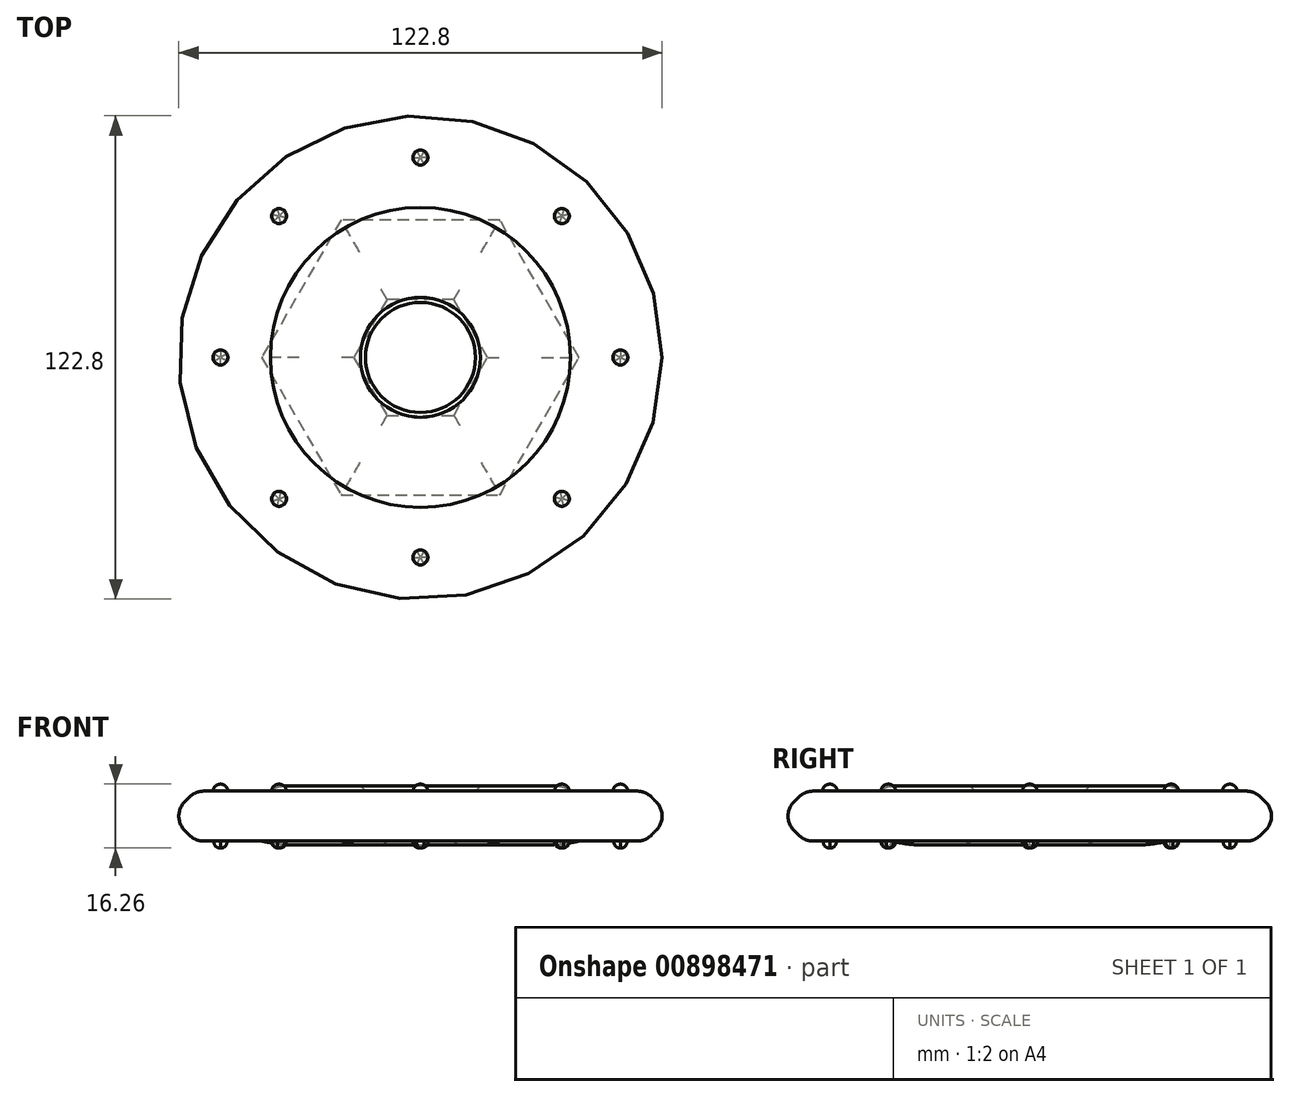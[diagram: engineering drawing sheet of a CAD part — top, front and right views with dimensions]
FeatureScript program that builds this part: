
annotation { "Feature Type Name" : "Feature", "Feature Type Description" : "" }
export const myFeature = defineFeature(function(context is Context, id is Id, definition is map)
    precondition{}
    {
        {
            var Q0;
            Q0=qCreatedBy(makeId("Top.planeOp"),FACE);
            var sketch = newSketch(context, id + "F0", { "sketchPlane" : qUnion([Q0])});
            skCircle(sketch, "E0", {"center": v(0, 0) * mm, "radius": 63.5 * mm});
            skSolve(sketch);
        }
        {
            var Q0;
            Q0=makeQuery(id+"F0.imprint","IMPRINT",FACE,{"disambiguationData":[TD([[makeQuery(id+"F0.imprint","IMPRINT",EDGE,{"derivedFrom":sQuery(id+"F0.wireOp",EDGE,"E0")}),1.0]])]});
            extrude(context, id + "F1", {"entities" : qUnion([Q0]), "depth" : 12.7 * mm, "offsetDistance" : 25.4 * mm});
        }
        {
            var Q0;
            Q0=makeQuery(id+"F1.opExtrude","CAP_FACE",FACE,{"disambiguationData":[OSD([sQuery(id+"F0.wireOp",EDGE,"E0")])],"isStart":false});
            var Q1;
            Q1=makeQuery(id+"F1.opExtrude","CAP_EDGE",EDGE,{"disambiguationData":[OSD([sQuery(id+"F0.wireOp",EDGE,"E0")])],"isStart":true});
            chamfer(context, id + "F2", {"entities" : qUnion([Q0, Q1]), "width" : 6.35 * mm, "tangentPropagation" : true});
        }
        {
            var Q0;
            Q0=makeQuery(id+"F1.opExtrude","CAP_FACE",FACE,{"disambiguationData":[OSD([sQuery(id+"F0.wireOp",EDGE,"E0")])],"isStart":false});
            fillet(context, id + "F3", {"entities" : qUnion([Q0]), "radius" : 5.08 * mm, "tangentPropagation" : true, "allowEdgeOverflow" : false});
        }
        {
            var Q0;
            {var subQ0=sQuery(id+"F0.wireOp",EDGE,"E0");Q0=makeQuery(id+"F2.opChamfer","BLEND_EDGE",EDGE,{"blendedFrom":[makeQuery(id+"F1.opExtrude","CAP_EDGE",EDGE,{"disambiguationData":[OSD([subQ0])],"isStart":true}),makeQuery(id+"F1.opExtrude","CAP_FACE",FACE,{"disambiguationData":[OSD([subQ0])],"isStart":true})],"blendedInto":[makeQuery(id+"F1.opExtrude","CAP_FACE",FACE,{"disambiguationData":[OSD([subQ0])],"isStart":true})]});}
            fillet(context, id + "F4", {"entities" : qUnion([Q0]), "radius" : 5.08 * mm, "tangentPropagation" : true, "allowEdgeOverflow" : false});
        }
        {
            var Q0;
            Q0=makeQuery(id+"F1.opExtrude","CAP_FACE",FACE,{"disambiguationData":[OSD([sQuery(id+"F0.wireOp",EDGE,"E0")])],"isStart":false});
            var sketch = newSketch(context, id + "F5", { "sketchPlane" : qUnion([Q0])});
            skLineSegment(sketch, "E1", {"start": v(0, 0) * mm, "end": v(0, 50.8) * mm, "construction": true});
            skCircle(sketch, "E2", {"center": v(0, 0) * mm, "radius": 50.8 * mm, "construction": true});
            skCircle(sketch, "E3", {"center": v(0, 50.8) * mm, "radius": 1.9 * mm});
            skLineSegment(sketch, "E4", {"start": v(-50.8, 0) * mm, "end": v(50.8, 0) * mm, "construction": true});
            skLineSegment(sketch, "E5", {"start": v(0, 0) * mm, "end": v(0, -50.8) * mm, "construction": true});
            skCircle(sketch, "E6", {"center": v(-50.8, 0) * mm, "radius": 1.9 * mm});
            skCircle(sketch, "E7", {"center": v(50.8, 0) * mm, "radius": 1.9 * mm});
            skCircle(sketch, "E8", {"center": v(0, -50.8) * mm, "radius": 1.9 * mm});
            skLineSegment(sketch, "E9", {"start": v(0, 0) * mm, "end": v(35.92, 35.92) * mm, "construction": true});
            skLineSegment(sketch, "E10", {"start": v(0, 0) * mm, "end": v(-35.92, 35.92) * mm, "construction": true});
            skLineSegment(sketch, "E11", {"start": v(-35.92, -35.92) * mm, "end": v(0, 0) * mm, "construction": true});
            skLineSegment(sketch, "E12", {"start": v(35.92, -35.92) * mm, "end": v(0, 0) * mm, "construction": true});
            skCircle(sketch, "E13", {"center": v(-35.92, 35.92) * mm, "radius": 1.9 * mm});
            skCircle(sketch, "E14", {"center": v(35.92, 35.92) * mm, "radius": 1.9 * mm});
            skCircle(sketch, "E15", {"center": v(35.92, -35.92) * mm, "radius": 1.9 * mm});
            skCircle(sketch, "E16", {"center": v(-35.92, -35.92) * mm, "radius": 1.9 * mm});
            skSolve(sketch);
        }
        {
            var Q0;
            Q0 = qSketchRegion(id + "F5", true);
            extrude(context, id + "F6", {"entities" : qUnion([Q0]), "operationType" : NewBodyOperationType.ADD, "depth" : 1.78 * mm, "offsetDistance" : 25.4 * mm});
        }
        {
            var Q0;
            Q0=makeQuery(id+"F6.opExtrude","CAP_EDGE",EDGE,{"disambiguationData":[OSD([sQuery(id+"F5.wireOp",EDGE,"E16")])],"isStart":false});
            var Q1;
            Q1=makeQuery(id+"F6.opExtrude","CAP_EDGE",EDGE,{"disambiguationData":[OSD([sQuery(id+"F5.wireOp",EDGE,"E6")])],"isStart":false});
            var Q2;
            Q2=makeQuery(id+"F6.opExtrude","CAP_EDGE",EDGE,{"disambiguationData":[OSD([sQuery(id+"F5.wireOp",EDGE,"E13")])],"isStart":false});
            var Q3;
            Q3=makeQuery(id+"F6.opExtrude","CAP_EDGE",EDGE,{"disambiguationData":[OSD([sQuery(id+"F5.wireOp",EDGE,"E3")])],"isStart":false});
            var Q4;
            Q4=makeQuery(id+"F6.opExtrude","CAP_EDGE",EDGE,{"disambiguationData":[OSD([sQuery(id+"F5.wireOp",EDGE,"E14")])],"isStart":false});
            var Q5;
            Q5=makeQuery(id+"F6.opExtrude","CAP_EDGE",EDGE,{"disambiguationData":[OSD([sQuery(id+"F5.wireOp",EDGE,"E7")])],"isStart":false});
            var Q6;
            Q6=makeQuery(id+"F6.opExtrude","CAP_EDGE",EDGE,{"disambiguationData":[OSD([sQuery(id+"F5.wireOp",EDGE,"E15")])],"isStart":false});
            var Q7;
            Q7=makeQuery(id+"F6.opExtrude","CAP_EDGE",EDGE,{"disambiguationData":[OSD([sQuery(id+"F5.wireOp",EDGE,"E8")])],"isStart":false});
            fillet(context, id + "F7", {"entities" : qUnion([Q0, Q1, Q2, Q3, Q4, Q5, Q6, Q7]), "radius" : 1.9 * mm, "tangentPropagation" : true, "allowEdgeOverflow" : false});
        }
        {
            var Q0;
            Q0=makeQuery(id+"F1.opExtrude","CAP_FACE",FACE,{"disambiguationData":[OSD([sQuery(id+"F0.wireOp",EDGE,"E0")])],"isStart":false});
            var sketch = newSketch(context, id + "F8", { "sketchPlane" : qUnion([Q0])});
            skCircle(sketch, "E17", {"center": v(0, 0) * mm, "radius": 38.1 * mm});
            skCircle(sketch, "E18", {"center": v(0, 0) * mm, "radius": 19.05 * mm});
            skSolve(sketch);
        }
        {
            var Q0;
            Q0 = qSketchRegion(id + "F8", true);
            extrude(context, id + "F9", {"entities" : qUnion([Q0]), "operationType" : NewBodyOperationType.ADD, "depth" : 1.27 * mm, "offsetDistance" : 25.4 * mm});
        }
        {
            var Q0;
            Q0=makeQuery(id+"F1.opExtrude","CAP_FACE",FACE,{"disambiguationData":[OSD([sQuery(id+"F0.wireOp",EDGE,"E0")])],"isStart":true});
            var sketch = newSketch(context, id + "F10", { "sketchPlane" : qUnion([Q0])});
            skCircle(sketch, "E19.cCircle", {"center": v(0, 0) * mm, "radius": 34.91 * mm, "construction": true});
            skLineSegment(sketch, "E19.0", {"start": v(20.16, -34.91) * mm, "end": v(-20.16, -34.91) * mm});
            skLineSegment(sketch, "E19.1", {"start": v(-20.16, -34.91) * mm, "end": v(-40.31, 0) * mm});
            skLineSegment(sketch, "E19.2", {"start": v(-40.31, 0) * mm, "end": v(-20.16, 34.91) * mm});
            skLineSegment(sketch, "E19.3", {"start": v(-20.16, 34.91) * mm, "end": v(20.16, 34.91) * mm});
            skLineSegment(sketch, "E19.4", {"start": v(20.16, 34.91) * mm, "end": v(40.31, 0) * mm});
            skLineSegment(sketch, "E19.5", {"start": v(40.31, 0) * mm, "end": v(20.16, -34.91) * mm});
            skPoint(sketch, "E19.0.midPoint", {"position": v(0, -34.91) * mm});
            skCircle(sketch, "E20.cCircle", {"center": v(0, 0) * mm, "radius": 14.71 * mm, "construction": true});
            skLineSegment(sketch, "E20.0", {"start": v(8.5, -14.71) * mm, "end": v(-8.5, -14.71) * mm});
            skLineSegment(sketch, "E20.1", {"start": v(-8.5, -14.71) * mm, "end": v(-17, 0) * mm});
            skLineSegment(sketch, "E20.2", {"start": v(-17, 0) * mm, "end": v(-8.5, 14.71) * mm});
            skLineSegment(sketch, "E20.3", {"start": v(-8.5, 14.71) * mm, "end": v(8.5, 14.71) * mm});
            skLineSegment(sketch, "E20.4", {"start": v(8.5, 14.71) * mm, "end": v(17, 0) * mm});
            skLineSegment(sketch, "E20.5", {"start": v(17, 0) * mm, "end": v(8.5, -14.71) * mm});
            skPoint(sketch, "E20.0.midPoint", {"position": v(0, -14.71) * mm});
            skSolve(sketch);
        }
        {
            var Q0;
            Q0 = qSketchRegion(id + "F10", true);
            extrude(context, id + "F11", {"entities" : qUnion([Q0]), "operationType" : NewBodyOperationType.ADD, "depth" : 1.02 * mm, "offsetDistance" : 25.4 * mm});
        }
        {
            var Q0;
            Q0=makeQuery(id+"F11.opExtrude","CAP_EDGE",EDGE,{"disambiguationData":[OSD([sQuery(id+"F10.wireOp",EDGE,"E19.1")])],"isStart":false});
            var Q1;
            Q1=makeQuery(id+"F11.opExtrude","CAP_EDGE",EDGE,{"disambiguationData":[OSD([sQuery(id+"F10.wireOp",EDGE,"E19.0")])],"isStart":false});
            var Q2;
            Q2=makeQuery(id+"F11.opExtrude","CAP_EDGE",EDGE,{"disambiguationData":[OSD([sQuery(id+"F10.wireOp",EDGE,"E19.5")])],"isStart":false});
            var Q3;
            Q3=makeQuery(id+"F11.opExtrude","CAP_EDGE",EDGE,{"disambiguationData":[OSD([sQuery(id+"F10.wireOp",EDGE,"E19.4")])],"isStart":false});
            var Q4;
            Q4=makeQuery(id+"F11.opExtrude","CAP_EDGE",EDGE,{"disambiguationData":[OSD([sQuery(id+"F10.wireOp",EDGE,"E19.3")])],"isStart":false});
            var Q5;
            Q5=makeQuery(id+"F11.opExtrude","CAP_EDGE",EDGE,{"disambiguationData":[OSD([sQuery(id+"F10.wireOp",EDGE,"E19.2")])],"isStart":false});
            fillet(context, id + "F12", {"entities" : qUnion([Q0, Q1, Q2, Q3, Q4, Q5]), "radius" : 33.78 * mm, "tangentPropagation" : true, "allowEdgeOverflow" : false});
        }
        {
            var Q0;
            Q0=makeQuery(id+"F9.opExtrude","CAP_EDGE",EDGE,{"disambiguationData":[OSD([sQuery(id+"F8.wireOp",EDGE,"E17")])],"isStart":false});
            fillet(context, id + "F13", {"entities" : qUnion([Q0]), "radius" : 5.08 * mm, "tangentPropagation" : true, "allowEdgeOverflow" : false});
        }
        {
            var Q0;
            Q0=makeQuery(id+"F9.boolean.opBoolean","SPLIT",FACE,{"disambiguationData":[TD([makeQuery(id+"F9.opExtrude","SWEPT_FACE",FACE,{"disambiguationData":[OSD([sQuery(id+"F8.wireOp",EDGE,"E18")])]})])],"derivedFrom":makeQuery(id+"F1.opExtrude","CAP_FACE",FACE,{"disambiguationData":[OSD([sQuery(id+"F0.wireOp",EDGE,"E0")])],"isStart":false})});
            chamfer(context, id + "F14", {"entities" : qUnion([Q0]), "width" : 5.08 * mm, "tangentPropagation" : true});
        }
        {
            var Q0;
            {var subQ0=sQuery(id+"F0.wireOp",EDGE,"E0");Q0=makeQuery(id+"F11.boolean.opBoolean","SPLIT",FACE,{"disambiguationData":[TD([makeQuery(id+"F4.opFillet","BLEND_FACE",FACE,{"disambiguationData":[OSD([subQ0])]})])],"derivedFrom":makeQuery(id+"F1.opExtrude","CAP_FACE",FACE,{"disambiguationData":[OSD([subQ0])],"isStart":true})});}
            var sketch = newSketch(context, id + "F15", { "sketchPlane" : qUnion([Q0])});
            skCircle(sketch, "E21", {"center": v(0, 0) * mm, "radius": 50.8 * mm, "construction": true});
            skCircle(sketch, "E22.cCircle", {"center": v(0, 50.8) * mm, "radius": 1.65 * mm, "construction": true});
            skLineSegment(sketch, "E22.0", {"start": v(0.95, 49.15) * mm, "end": v(-0.95, 49.15) * mm});
            skLineSegment(sketch, "E22.1", {"start": v(-0.95, 49.15) * mm, "end": v(-1.9, 50.8) * mm});
            skLineSegment(sketch, "E22.2", {"start": v(-1.9, 50.8) * mm, "end": v(-0.95, 52.45) * mm});
            skLineSegment(sketch, "E22.3", {"start": v(-0.95, 52.45) * mm, "end": v(0.95, 52.45) * mm});
            skLineSegment(sketch, "E22.4", {"start": v(0.95, 52.45) * mm, "end": v(1.9, 50.8) * mm});
            skLineSegment(sketch, "E22.5", {"start": v(1.9, 50.8) * mm, "end": v(0.95, 49.15) * mm});
            skPoint(sketch, "E22.0.midPoint", {"position": v(0, 49.15) * mm});
            skCircle(sketch, "E23.cCircle", {"center": v(35.92, 35.92) * mm, "radius": 1.65 * mm, "construction": true});
            skLineSegment(sketch, "E23.0", {"start": v(35.43, 34.08) * mm, "end": v(34.08, 35.43) * mm});
            skLineSegment(sketch, "E23.1", {"start": v(34.08, 35.43) * mm, "end": v(34.57, 37.27) * mm});
            skLineSegment(sketch, "E23.2", {"start": v(34.57, 37.27) * mm, "end": v(36.41, 37.76) * mm});
            skLineSegment(sketch, "E23.3", {"start": v(36.41, 37.76) * mm, "end": v(37.76, 36.41) * mm});
            skLineSegment(sketch, "E23.4", {"start": v(37.76, 36.41) * mm, "end": v(37.27, 34.57) * mm});
            skLineSegment(sketch, "E23.5", {"start": v(37.27, 34.57) * mm, "end": v(35.43, 34.08) * mm});
            skPoint(sketch, "E23.0.midPoint", {"position": v(34.75, 34.75) * mm});
            skCircle(sketch, "E24.cCircle", {"center": v(50.8, 0) * mm, "radius": 1.65 * mm, "construction": true});
            skLineSegment(sketch, "E24.0", {"start": v(49.15, -0.95) * mm, "end": v(49.15, 0.95) * mm});
            skLineSegment(sketch, "E24.1", {"start": v(49.15, 0.95) * mm, "end": v(50.8, 1.9) * mm});
            skLineSegment(sketch, "E24.2", {"start": v(50.8, 1.9) * mm, "end": v(52.45, 0.95) * mm});
            skLineSegment(sketch, "E24.3", {"start": v(52.45, 0.95) * mm, "end": v(52.45, -0.95) * mm});
            skLineSegment(sketch, "E24.4", {"start": v(52.45, -0.95) * mm, "end": v(50.8, -1.9) * mm});
            skLineSegment(sketch, "E24.5", {"start": v(50.8, -1.9) * mm, "end": v(49.15, -0.95) * mm});
            skPoint(sketch, "E24.0.midPoint", {"position": v(49.15, 0) * mm});
            skPoint(sketch, "E25.0.midPoint", {"position": v(34.75, -32.79) * mm});
            skCircle(sketch, "E26.cCircle", {"center": v(-50.8, 0) * mm, "radius": 1.65 * mm, "construction": true});
            skLineSegment(sketch, "E26.0", {"start": v(-49.15, 0.95) * mm, "end": v(-49.15, -0.95) * mm});
            skLineSegment(sketch, "E26.1", {"start": v(-49.15, -0.95) * mm, "end": v(-50.8, -1.9) * mm});
            skLineSegment(sketch, "E26.2", {"start": v(-50.8, -1.9) * mm, "end": v(-52.45, -0.95) * mm});
            skLineSegment(sketch, "E26.3", {"start": v(-52.45, -0.95) * mm, "end": v(-52.45, 0.95) * mm});
            skLineSegment(sketch, "E26.4", {"start": v(-52.45, 0.95) * mm, "end": v(-50.8, 1.9) * mm});
            skLineSegment(sketch, "E26.5", {"start": v(-50.8, 1.9) * mm, "end": v(-49.15, 0.95) * mm});
            skPoint(sketch, "E26.0.midPoint", {"position": v(-49.15, 0) * mm});
            skCircle(sketch, "E27.cCircle", {"center": v(0, -50.8) * mm, "radius": 1.65 * mm, "construction": true});
            skLineSegment(sketch, "E27.0", {"start": v(-0.95, -49.15) * mm, "end": v(0.95, -49.15) * mm});
            skLineSegment(sketch, "E27.1", {"start": v(0.95, -49.15) * mm, "end": v(1.9, -50.8) * mm});
            skLineSegment(sketch, "E27.2", {"start": v(1.9, -50.8) * mm, "end": v(0.95, -52.45) * mm});
            skLineSegment(sketch, "E27.3", {"start": v(0.95, -52.45) * mm, "end": v(-0.95, -52.45) * mm});
            skLineSegment(sketch, "E27.4", {"start": v(-0.95, -52.45) * mm, "end": v(-1.9, -50.8) * mm});
            skLineSegment(sketch, "E27.5", {"start": v(-1.9, -50.8) * mm, "end": v(-0.95, -49.15) * mm});
            skPoint(sketch, "E27.0.midPoint", {"position": v(0, -49.15) * mm});
            skLineSegment(sketch, "E28", {"start": v(-1.9, -50.8) * mm, "end": v(1.9, -50.8) * mm, "construction": true});
            skCircle(sketch, "E29.cCircle", {"center": v(35.92, -35.92) * mm, "radius": 1.65 * mm, "construction": true});
            skLineSegment(sketch, "E29.0", {"start": v(37.76, -36.41) * mm, "end": v(36.41, -37.76) * mm});
            skLineSegment(sketch, "E29.1", {"start": v(36.41, -37.76) * mm, "end": v(34.57, -37.27) * mm});
            skLineSegment(sketch, "E29.2", {"start": v(34.57, -37.27) * mm, "end": v(34.08, -35.43) * mm});
            skLineSegment(sketch, "E29.3", {"start": v(34.08, -35.43) * mm, "end": v(35.43, -34.08) * mm});
            skLineSegment(sketch, "E29.4", {"start": v(35.43, -34.08) * mm, "end": v(37.27, -34.57) * mm});
            skLineSegment(sketch, "E29.5", {"start": v(37.27, -34.57) * mm, "end": v(37.76, -36.41) * mm});
            skPoint(sketch, "E29.0.midPoint", {"position": v(37.09, -37.09) * mm});
            skPoint(sketch, "E30.0.midPoint", {"position": v(-34.7, -37.03) * mm});
            skPoint(sketch, "E30.0.midPoint.positionSnap0", {"position": v(-34.7, -40.48) * mm});
            skCircle(sketch, "E31.cCircle", {"center": v(-35.92, 35.92) * mm, "radius": 1.65 * mm, "construction": true});
            skLineSegment(sketch, "E31.0", {"start": v(-34.1, 35.37) * mm, "end": v(-35.49, 34.07) * mm});
            skLineSegment(sketch, "E31.1", {"start": v(-35.49, 34.07) * mm, "end": v(-37.3, 34.62) * mm});
            skLineSegment(sketch, "E31.2", {"start": v(-37.3, 34.62) * mm, "end": v(-37.74, 36.47) * mm});
            skLineSegment(sketch, "E31.3", {"start": v(-37.74, 36.47) * mm, "end": v(-36.36, 37.78) * mm});
            skLineSegment(sketch, "E31.4", {"start": v(-36.36, 37.78) * mm, "end": v(-34.53, 37.23) * mm});
            skLineSegment(sketch, "E31.5", {"start": v(-34.53, 37.23) * mm, "end": v(-34.1, 35.37) * mm});
            skPoint(sketch, "E31.0.midPoint", {"position": v(-34.8, 34.72) * mm});
            skCircle(sketch, "E32.cCircle", {"center": v(-35.92, -35.92) * mm, "radius": 1.65 * mm, "construction": true});
            skLineSegment(sketch, "E32.0", {"start": v(-35.44, -34.08) * mm, "end": v(-34.09, -35.41) * mm});
            skLineSegment(sketch, "E32.1", {"start": v(-34.09, -35.41) * mm, "end": v(-34.56, -37.26) * mm});
            skLineSegment(sketch, "E32.2", {"start": v(-34.56, -37.26) * mm, "end": v(-36.4, -37.77) * mm});
            skLineSegment(sketch, "E32.3", {"start": v(-36.4, -37.77) * mm, "end": v(-37.76, -36.43) * mm});
            skLineSegment(sketch, "E32.4", {"start": v(-37.76, -36.43) * mm, "end": v(-37.28, -34.59) * mm});
            skLineSegment(sketch, "E32.5", {"start": v(-37.28, -34.59) * mm, "end": v(-35.44, -34.08) * mm});
            skPoint(sketch, "E32.0.midPoint", {"position": v(-34.76, -34.74) * mm});
            skSolve(sketch);
        }
        {
            var Q0;
            Q0 = qSketchRegion(id + "F15", true);
            extrude(context, id + "F16", {"entities" : qUnion([Q0]), "operationType" : NewBodyOperationType.ADD, "depth" : 1.78 * mm, "offsetDistance" : 25.4 * mm});
        }
        {
            var Q0;
            Q0=makeQuery(id+"F16.opExtrude","CAP_FACE",FACE,{"disambiguationData":[OSD([sQuery(id+"F15.wireOp",EDGE,"E27.0"),sQuery(id+"F15.wireOp",EDGE,"E27.1"),sQuery(id+"F15.wireOp",EDGE,"E27.2"),sQuery(id+"F15.wireOp",EDGE,"E27.3"),sQuery(id+"F15.wireOp",EDGE,"E27.4"),sQuery(id+"F15.wireOp",EDGE,"E27.5")])],"isStart":false});
            var Q1;
            Q1=makeQuery(id+"F16.opExtrude","CAP_FACE",FACE,{"disambiguationData":[OSD([sQuery(id+"F15.wireOp",EDGE,"E29.0"),sQuery(id+"F15.wireOp",EDGE,"E29.1"),sQuery(id+"F15.wireOp",EDGE,"E29.2"),sQuery(id+"F15.wireOp",EDGE,"E29.3"),sQuery(id+"F15.wireOp",EDGE,"E29.4"),sQuery(id+"F15.wireOp",EDGE,"E29.5")])],"isStart":false});
            var Q2;
            Q2=makeQuery(id+"F16.opExtrude","CAP_FACE",FACE,{"disambiguationData":[OSD([sQuery(id+"F15.wireOp",EDGE,"E24.0"),sQuery(id+"F15.wireOp",EDGE,"E24.1"),sQuery(id+"F15.wireOp",EDGE,"E24.2"),sQuery(id+"F15.wireOp",EDGE,"E24.3"),sQuery(id+"F15.wireOp",EDGE,"E24.4"),sQuery(id+"F15.wireOp",EDGE,"E24.5")])],"isStart":false});
            var Q3;
            Q3=makeQuery(id+"F16.opExtrude","CAP_FACE",FACE,{"disambiguationData":[OSD([sQuery(id+"F15.wireOp",EDGE,"E23.0"),sQuery(id+"F15.wireOp",EDGE,"E23.1"),sQuery(id+"F15.wireOp",EDGE,"E23.2"),sQuery(id+"F15.wireOp",EDGE,"E23.3"),sQuery(id+"F15.wireOp",EDGE,"E23.4"),sQuery(id+"F15.wireOp",EDGE,"E23.5")])],"isStart":false});
            var Q4;
            Q4=makeQuery(id+"F16.opExtrude","CAP_FACE",FACE,{"disambiguationData":[OSD([sQuery(id+"F15.wireOp",EDGE,"E22.0"),sQuery(id+"F15.wireOp",EDGE,"E22.1"),sQuery(id+"F15.wireOp",EDGE,"E22.2"),sQuery(id+"F15.wireOp",EDGE,"E22.3"),sQuery(id+"F15.wireOp",EDGE,"E22.4"),sQuery(id+"F15.wireOp",EDGE,"E22.5")])],"isStart":false});
            var Q5;
            Q5=makeQuery(id+"F16.opExtrude","CAP_FACE",FACE,{"disambiguationData":[OSD([sQuery(id+"F15.wireOp",EDGE,"E31.0"),sQuery(id+"F15.wireOp",EDGE,"E31.1"),sQuery(id+"F15.wireOp",EDGE,"E31.2"),sQuery(id+"F15.wireOp",EDGE,"E31.3"),sQuery(id+"F15.wireOp",EDGE,"E31.4"),sQuery(id+"F15.wireOp",EDGE,"E31.5")])],"isStart":false});
            var Q6;
            Q6=makeQuery(id+"F16.opExtrude","CAP_FACE",FACE,{"disambiguationData":[OSD([sQuery(id+"F15.wireOp",EDGE,"E32.0"),sQuery(id+"F15.wireOp",EDGE,"E32.1"),sQuery(id+"F15.wireOp",EDGE,"E32.2"),sQuery(id+"F15.wireOp",EDGE,"E32.3"),sQuery(id+"F15.wireOp",EDGE,"E32.4"),sQuery(id+"F15.wireOp",EDGE,"E32.5")])],"isStart":false});
            var Q7;
            Q7=makeQuery(id+"F16.opExtrude","CAP_FACE",FACE,{"disambiguationData":[OSD([sQuery(id+"F15.wireOp",EDGE,"E26.0"),sQuery(id+"F15.wireOp",EDGE,"E26.1"),sQuery(id+"F15.wireOp",EDGE,"E26.2"),sQuery(id+"F15.wireOp",EDGE,"E26.3"),sQuery(id+"F15.wireOp",EDGE,"E26.4"),sQuery(id+"F15.wireOp",EDGE,"E26.5")])],"isStart":false});
            fillet(context, id + "F17", {"entities" : qUnion([Q0, Q1, Q2, Q3, Q4, Q5, Q6, Q7]), "radius" : 1.53 * mm, "tangentPropagation" : true, "allowEdgeOverflow" : false});
        }
        {
            var Q0;
            Q0=makeQuery(id+"F11.opExtrude","CAP_EDGE",EDGE,{"disambiguationData":[OSD([sQuery(id+"F10.wireOp",EDGE,"E20.3")])],"isStart":false});
            var Q1;
            Q1=makeQuery(id+"F11.opExtrude","CAP_EDGE",EDGE,{"disambiguationData":[OSD([sQuery(id+"F10.wireOp",EDGE,"E20.4")])],"isStart":false});
            var Q2;
            Q2=makeQuery(id+"F11.opExtrude","CAP_EDGE",EDGE,{"disambiguationData":[OSD([sQuery(id+"F10.wireOp",EDGE,"E20.5")])],"isStart":false});
            var Q3;
            Q3=makeQuery(id+"F11.opExtrude","CAP_EDGE",EDGE,{"disambiguationData":[OSD([sQuery(id+"F10.wireOp",EDGE,"E20.0")])],"isStart":false});
            var Q4;
            Q4=makeQuery(id+"F11.opExtrude","CAP_EDGE",EDGE,{"disambiguationData":[OSD([sQuery(id+"F10.wireOp",EDGE,"E20.1")])],"isStart":false});
            var Q5;
            Q5=makeQuery(id+"F11.opExtrude","CAP_EDGE",EDGE,{"disambiguationData":[OSD([sQuery(id+"F10.wireOp",EDGE,"E20.2")])],"isStart":false});
            fillet(context, id + "F18", {"entities" : qUnion([Q0, Q1, Q2, Q3, Q4, Q5]), "radius" : 5.08 * mm, "tangentPropagation" : true, "allowEdgeOverflow" : false});
        }
        {
            var Q0;
            {var subQ0=sQuery(id+"F0.wireOp",EDGE,"E0");Q0=makeQuery(id+"F2.opChamfer","BLEND_EDGE",EDGE,{"blendedFrom":[makeQuery(id+"F1.opExtrude","CAP_EDGE",EDGE,{"disambiguationData":[OSD([subQ0])],"isStart":true}),makeQuery(id+"F1.opExtrude","CAP_EDGE",EDGE,{"disambiguationData":[OSD([subQ0])],"isStart":false})],"blendedInto":[]});}
            fillet(context, id + "F19", {"entities" : qUnion([Q0]), "radius" : 5.08 * mm, "tangentPropagation" : true, "allowEdgeOverflow" : false});
        }
    });
